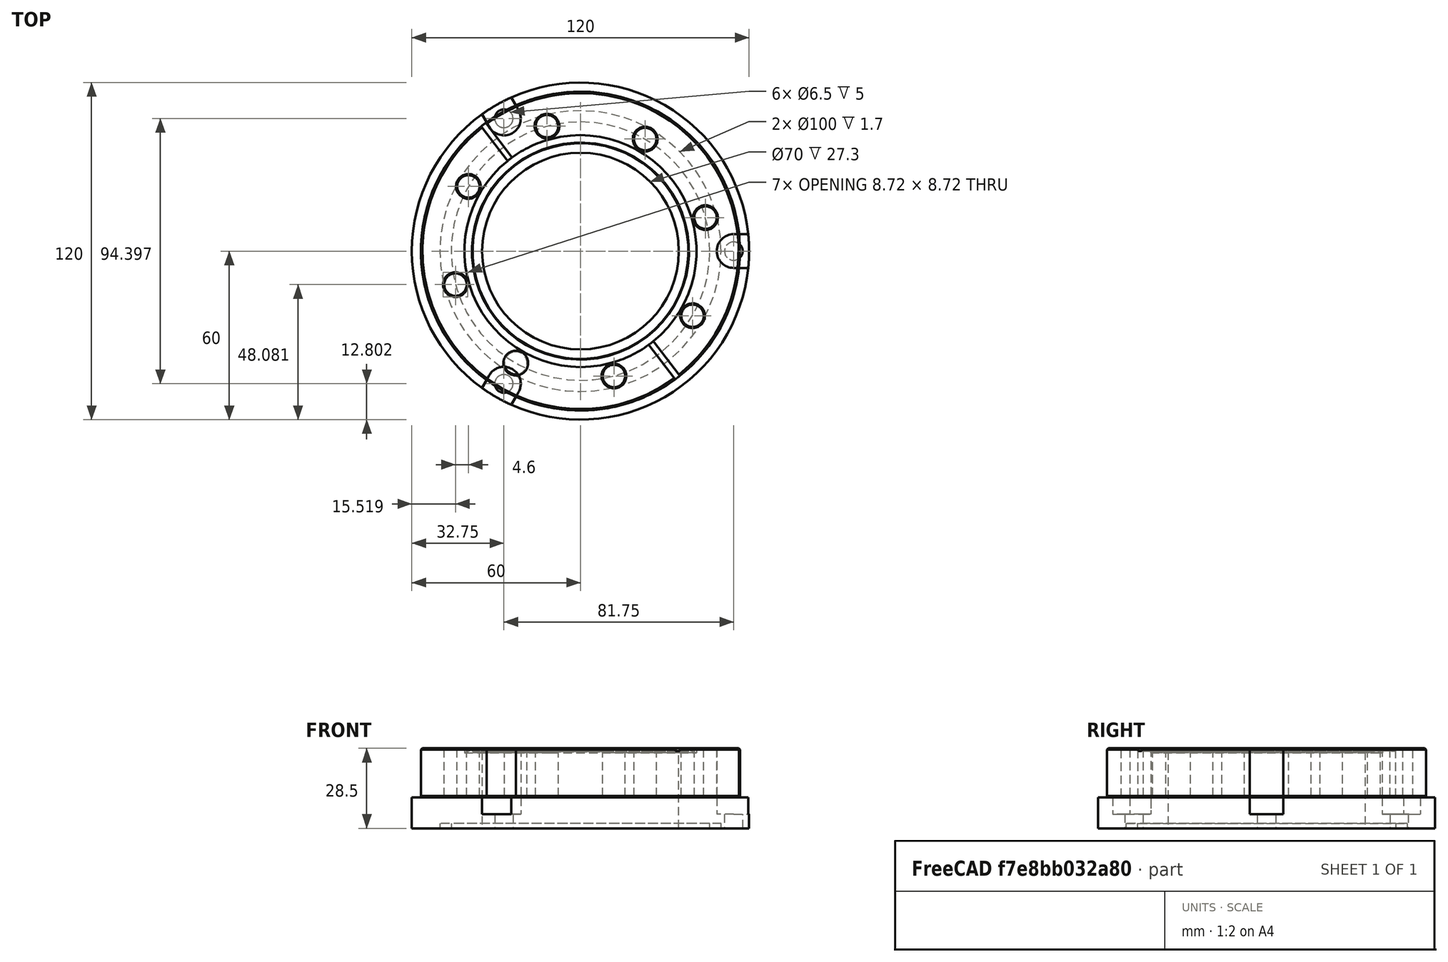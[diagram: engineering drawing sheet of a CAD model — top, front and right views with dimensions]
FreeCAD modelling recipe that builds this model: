
FCSTD DOCUMENT  (FreeCAD 0.21R33675 (Git))
Label: PhilippsXL30_FlangeToCF63_ZeroLengthAdapter_100
License: All rights reserved
LicenseURL: http://en.wikipedia.org/wiki/All_rights_reserved
objects: TechDraw::DrawViewDimension×32, Part::Cylinder×5, Part::MultiFuse×5, Part::Box×3, Part::Feature×3, Part::Compound×3, TechDraw::DrawProjGroupItem×3, TechDraw::DrawSVGTemplate×2, Part::Cut×2, TechDraw::DrawPage×2, App::Link×1, TechDraw::DrawProjGroup×1, TechDraw::DrawViewPart×1, TechDraw::DrawViewSection×1
note: 65 computed .brp shape members not serialized (recipe doc carries the construction recipe); baked Part::Feature solids carry a one-line shape summary decoded from their .brp
EXTERNAL_REF file=PhilippsXL30_Blindflange_120.FCStd obj=Cut003

FEATURE [App::Link] Link  label="Cut003"
  LinkedObject = -> <external PhilippsXL30_Blindflange_120.FCStd>#Cut003
FEATURE [Part::Box] Box  label="Würfel"
  AttacherType = Attacher::AttachEngine3D
  Height = 24
  Length = 10
  Placement = pos=(54.5,-6,5) rot=(0,0,1;0rad)
  Width = 12
FEATURE [Part::Cylinder] Cylinder  label="Zylinder"
  Angle = 360
  AttacherType = Attacher::AttachEngine3D
  FirstAngle = 0
  Height = 24
  Placement = pos=(54.5,0,5) rot=(0,0,1;0rad)
  Radius = 6
  SecondAngle = 0
FEATURE [Part::Box] Box001  label="Würfel001"
  AttacherType = Attacher::AttachEngine3D
  Height = 24
  Length = 10
  Placement = pos=(54.5,-6,5) rot=(0,0,1;0rad)
  Width = 12
FEATURE [Part::Cylinder] Cylinder001  label="Zylinder001"
  Angle = 360
  AttacherType = Attacher::AttachEngine3D
  FirstAngle = 0
  Height = 24
  Placement = pos=(54.5,0,5) rot=(0,0,1;0rad)
  Radius = 6
  SecondAngle = 0
FEATURE [Part::Box] Box002  label="Würfel002"
  AttacherType = Attacher::AttachEngine3D
  Height = 24
  Length = 10
  Placement = pos=(54.5,-6,5) rot=(0,0,1;0rad)
  Width = 12
FEATURE [Part::Cylinder] Cylinder002  label="Zylinder002"
  Angle = 360
  AttacherType = Attacher::AttachEngine3D
  FirstAngle = 0
  Height = 24
  Placement = pos=(54.5,0,5) rot=(0,0,1;0rad)
  Radius = 6
  SecondAngle = 0
FEATURE [Part::Feature] Link_solid  label="Cut003 (Solid)"
  shape: bbox 120 x 120 x 11 mm, 31 faces (baked)
FEATURE [Part::MultiFuse] Fusion001
  Shapes = -> [Box,Cylinder]
FEATURE [Part::MultiFuse] Fusion002
  Placement = pos=(0,0,0) rot=(0,0,1;2.0944rad)
  Shapes = -> [Box001,Cylinder001]
FEATURE [Part::MultiFuse] Fusion003
  Placement = pos=(0,0,0) rot=(0,0,1;4.18879rad)
  Shapes = -> [Box002,Cylinder002]
FEATURE [Part::Compound] Compound001
  Links = -> [Fusion001,Fusion002,Fusion003]
FEATURE [Part::Cylinder] Cylinder003  label="Zylinder003"
  Angle = 360
  AttacherType = Attacher::AttachEngine3D
  FirstAngle = 0
  Height = 23.5
  Placement = pos=(46.1,0,5) rot=(0,0,1;0rad)
  Radius = 4.8
  SecondAngle = 0
FEATURE [Part::Compound] Compound002
  Links = -> [Cylinder003]
  Placement = pos=(0,0,0) rot=(0,0,1;4.18879rad)
FEATURE [Part::Cylinder] Cylinder004  label="Zylinder004"
  Angle = 360
  AttacherType = Attacher::AttachEngine3D
  FirstAngle = 0
  Height = 50
  Radius = 35
  SecondAngle = 0
FEATURE [TechDraw::DrawSVGTemplate] Template
  EditableTexts = Designed_by_Name=Thomas Spielauer; FC-Date=2023-11-08; FC-SC=mm; FC-SH=1/2; FC-Title=120mm to CF63 adapter; Subtitle=XL30 ESEM compatible
  Height = 210
  Orientation = 1
  Template = <path>
  Width = 297
FEATURE [Part::Feature] Part__Feature001  label="Hositrad_CF63-BT"
  Placement = pos=(0,0,28.5) rot=(1,0,0;1.5708rad)
  shape: bbox 113.5 x 113.5 x 17.5 mm, 71 faces (baked)
FEATURE [Part::Compound] Compound
  Links = -> [Part__Feature001]
  Placement = pos=(0,0,0) rot=(0,0,1;0.261799rad)
FEATURE [Part::MultiFuse] Fusion
  Shapes = -> [Link_solid,Compound]
FEATURE [Part::Feature] Fusion_solid001  label="Fusion (Solid)001"
  shape: bbox 120 x 120 x 28.5 mm, 114 faces (baked)
FEATURE [Part::MultiFuse] Fusion004
  Shapes = -> [Compound002,Fusion_solid001]
FEATURE [Part::Cut] Cut
  Base = -> Fusion004
  Tool = -> Compound001
FEATURE [Part::Cut] Cut001
  Base = -> Cut
  Tool = -> Cylinder004
FEATURE [TechDraw::DrawProjGroupItem] ProjItem  label="Front"
  CoarseView = false
  Direction = (0,0,-1)
  Focus = 100
  HardHidden = false
  IsoCount = 0
  IsoHidden = false
  IsoVisible = false
  LockPosition = true
  Perspective = false
  Rotation = 0
  RotationVector = (0,1,0)
  Scale = 0.666667
  ScaleType = 2
  ScrubCount = 0
  SeamHidden = false
  SeamVisible = false
  SmoothHidden = false
  SmoothVisible = true
  Source = -> [Cut001]
  Type = 0
  X = 0
  XDirection = (0,1,0)
  Y = 0
FEATURE [TechDraw::DrawProjGroupItem] ProjItem001  label="Rear"
  CoarseView = false
  Direction = (0,0,1)
  Focus = 100
  HardHidden = false
  IsoCount = 0
  IsoHidden = false
  IsoVisible = false
  LockPosition = false
  Perspective = false
  Rotation = 0
  RotationVector = (1,0,0)
  Scale = 0.666667
  ScaleType = 2
  ScrubCount = 0
  SeamHidden = false
  SeamVisible = false
  SmoothHidden = false
  SmoothVisible = true
  Source = -> [Cut001]
  Type = 3
  X = 103.585
  XDirection = (0,-1,0)
  Y = 0
FEATURE [TechDraw::DrawProjGroupItem] ProjItem002  label="Top"
  CoarseView = false
  Direction = (1,0,0)
  Focus = 100
  HardHidden = false
  IsoCount = 0
  IsoHidden = false
  IsoVisible = false
  LockPosition = false
  Perspective = false
  Rotation = 0
  RotationVector = (1,0,0)
  Scale = 0.666667
  ScaleType = 2
  ScrubCount = 0
  SeamHidden = false
  SeamVisible = false
  SmoothHidden = false
  SmoothVisible = true
  Source = -> [Cut001]
  Type = 4
  X = 0
  XDirection = (0,1,0)
  Y = -91.1591
FEATURE [TechDraw::DrawProjGroup] ProjGroup
  Anchor = -> ProjItem
  AutoDistribute = false
  LockPosition = false
  ProjectionType = 0
  Rotation = 0
  Scale = 0.666667
  ScaleType = 2
  Source = -> [Cut001]
  Views = -> [ProjItem,ProjItem001,ProjItem002]
  X = 86.4871
  Y = 141.809
  spacingX = 15
  spacingY = 15
FEATURE [TechDraw::DrawViewDimension] Dimension
  AngleOverride = false
  Arbitrary = false
  ArbitraryTolerances = false
  EqualTolerance = true
  ExtensionAngle = 0
  FormatSpec = ⌀%.2w
  FormatSpecOverTolerance = %+.2w
  FormatSpecUnderTolerance = %+.2w
  Inverted = false
  LineAngle = 0
  LockPosition = false
  MeasureType = 1
  OverTolerance = 0
  References2D = -> [ProjItem]
  Rotation = 0
  ScaleType = 0
  TheoreticalExact = false
  Type = 5
  UnderTolerance = 0
  X = 13.273
  Y = 49.9319
FEATURE [TechDraw::DrawViewDimension] Dimension001
  AngleOverride = false
  Arbitrary = false
  ArbitraryTolerances = false
  EqualTolerance = true
  ExtensionAngle = 0
  FormatSpec = ⌀%.2w
  FormatSpecOverTolerance = %+.2w
  FormatSpecUnderTolerance = %+.2w
  Inverted = false
  LineAngle = 0
  LockPosition = false
  MeasureType = 1
  OverTolerance = 0
  References2D = -> [ProjItem]
  Rotation = 0
  ScaleType = 0
  TheoreticalExact = false
  Type = 5
  UnderTolerance = 0
  X = 24.0179
  Y = 47.193
FEATURE [TechDraw::DrawViewDimension] Dimension002
  AngleOverride = false
  Arbitrary = false
  ArbitraryTolerances = false
  EqualTolerance = true
  ExtensionAngle = 0
  FormatSpec = ⌀%.2w
  FormatSpecOverTolerance = %+.2w
  FormatSpecUnderTolerance = %+.2w
  Inverted = false
  LineAngle = 0
  LockPosition = false
  MeasureType = 1
  OverTolerance = 0
  References2D = -> [ProjItem]
  Rotation = 0
  ScaleType = 0
  TheoreticalExact = false
  Type = 5
  UnderTolerance = 0
  X = 30.1277
  Y = 42.7687
FEATURE [TechDraw::DrawViewDimension] Dimension003
  AngleOverride = false
  Arbitrary = false
  ArbitraryTolerances = false
  EqualTolerance = true
  ExtensionAngle = 0
  FormatSpec = ⌀%.2w
  FormatSpecOverTolerance = %+.2w
  FormatSpecUnderTolerance = %+.2w
  Inverted = false
  LineAngle = 0
  LockPosition = false
  MeasureType = 1
  OverTolerance = 0
  References2D = -> [ProjItem]
  Rotation = 0
  ScaleType = 0
  TheoreticalExact = false
  Type = 5
  UnderTolerance = 0
  X = 35.1841
  Y = 34.552
FEATURE [TechDraw::DrawViewDimension] Dimension004
  AngleOverride = false
  Arbitrary = false
  ArbitraryTolerances = false
  EqualTolerance = true
  ExtensionAngle = 0
  FormatSpec = ⌀%.2w
  FormatSpecOverTolerance = %+.2w
  FormatSpecUnderTolerance = %+.2w
  Inverted = false
  LineAngle = 0
  LockPosition = false
  MeasureType = 1
  OverTolerance = 0
  References2D = -> [ProjItem]
  Rotation = 0
  ScaleType = 0
  TheoreticalExact = false
  Type = 5
  UnderTolerance = 0
  X = 47.761
  Y = 10.7853
FEATURE [TechDraw::DrawViewDimension] Dimension005
  AngleOverride = false
  Arbitrary = false
  ArbitraryTolerances = false
  EqualTolerance = true
  ExtensionAngle = 0
  FormatSpec = %.2w
  FormatSpecOverTolerance = %+.2w
  FormatSpecUnderTolerance = %+.2w
  Inverted = false
  LineAngle = 0
  LockPosition = false
  MeasureType = 1
  OverTolerance = 0
  References2D = -> [ProjItem]
  Rotation = 0
  ScaleType = 0
  TheoreticalExact = false
  Type = 6
  UnderTolerance = 0
  X = 30.5032
  Y = -36.3658
FEATURE [TechDraw::DrawViewDimension] Dimension006
  AngleOverride = false
  Arbitrary = false
  ArbitraryTolerances = false
  EqualTolerance = true
  ExtensionAngle = 0
  FormatSpec = ⌀%.2w (3x)
  FormatSpecOverTolerance = %+.2w
  FormatSpecUnderTolerance = %+.2w
  Inverted = false
  LineAngle = 0
  LockPosition = false
  MeasureType = 1
  OverTolerance = 0
  References2D = -> [ProjItem]
  Rotation = 0
  ScaleType = 0
  TheoreticalExact = false
  Type = 5
  UnderTolerance = 0
  X = -27.3798
  Y = 53.7456
FEATURE [TechDraw::DrawViewDimension] Dimension007
  AngleOverride = false
  Arbitrary = false
  ArbitraryTolerances = false
  EqualTolerance = true
  ExtensionAngle = 0
  FormatSpec = ⌀%.2w
  FormatSpecOverTolerance = %+.2w
  FormatSpecUnderTolerance = %+.2w
  Inverted = false
  LineAngle = 0
  LockPosition = false
  MeasureType = 1
  OverTolerance = 0
  References2D = -> [ProjItem001]
  Rotation = 0
  ScaleType = 0
  TheoreticalExact = false
  Type = 5
  UnderTolerance = 0
  X = 51.25
  Y = 21.5576
FEATURE [TechDraw::DrawViewDimension] Dimension008
  AngleOverride = false
  Arbitrary = false
  ArbitraryTolerances = false
  EqualTolerance = true
  ExtensionAngle = 0
  FormatSpec = ⌀%.2w (CF63 knife)
  FormatSpecOverTolerance = %+.2w
  FormatSpecUnderTolerance = %+.2w
  Inverted = false
  LineAngle = 0
  LockPosition = false
  MeasureType = 1
  OverTolerance = 0
  References2D = -> [ProjItem001]
  Rotation = 0
  ScaleType = 0
  TheoreticalExact = false
  Type = 5
  UnderTolerance = 0
  X = 68.2486
  Y = 15.1076
FEATURE [TechDraw::DrawViewDimension] Dimension010
  AngleOverride = false
  Arbitrary = false
  ArbitraryTolerances = false
  EqualTolerance = true
  ExtensionAngle = 0
  FormatSpec = ⌀%.2w
  FormatSpecOverTolerance = %+.2w
  FormatSpecUnderTolerance = %+.2w
  Inverted = false
  LineAngle = 0
  LockPosition = false
  MeasureType = 1
  OverTolerance = 0
  References2D = -> [ProjItem001]
  Rotation = 0
  ScaleType = 0
  TheoreticalExact = false
  Type = 5
  UnderTolerance = 0
  X = 50.7383
  Y = -4.01857
FEATURE [TechDraw::DrawViewDimension] Dimension011
  AngleOverride = false
  Arbitrary = false
  ArbitraryTolerances = false
  EqualTolerance = true
  ExtensionAngle = 0
  FormatSpec = ⌀%+2w (7x M8)
  FormatSpecOverTolerance = %+.2w
  FormatSpecUnderTolerance = %+.2w
  Inverted = false
  LineAngle = 0
  LockPosition = false
  MeasureType = 1
  OverTolerance = 0
  References2D = -> [ProjItem001]
  Rotation = 0
  ScaleType = 0
  TheoreticalExact = false
  Type = 5
  UnderTolerance = 0
  X = 44.1386
  Y = 45.7398
FEATURE [TechDraw::DrawViewDimension] Dimension012
  AngleOverride = false
  Arbitrary = false
  ArbitraryTolerances = false
  EqualTolerance = true
  ExtensionAngle = 0
  FormatSpec = ⌀%.2w (ignore)
  FormatSpecOverTolerance = %+.2w
  FormatSpecUnderTolerance = %+.2w
  Inverted = false
  LineAngle = 0
  LockPosition = false
  MeasureType = 1
  OverTolerance = 0
  References2D = -> [ProjItem001]
  Rotation = 0
  ScaleType = 0
  TheoreticalExact = false
  Type = 5
  UnderTolerance = 0
  X = 56.2438
  Y = -18.0288
FEATURE [TechDraw::DrawViewDimension] Dimension013
  AngleOverride = false
  Arbitrary = false
  ArbitraryTolerances = false
  EqualTolerance = true
  ExtensionAngle = 0
  FormatSpec = ⌀%.2w (CF63 knife)
  FormatSpecOverTolerance = %+.2w
  FormatSpecUnderTolerance = %+.2w
  Inverted = false
  LineAngle = 0
  LockPosition = false
  MeasureType = 1
  OverTolerance = 0
  References2D = -> [ProjItem001]
  Rotation = 0
  ScaleType = 0
  TheoreticalExact = false
  Type = 5
  UnderTolerance = 0
  X = 69.1563
  Y = 3.81479
FEATURE [TechDraw::DrawViewDimension] Dimension014
  AngleOverride = false
  Arbitrary = false
  ArbitraryTolerances = false
  EqualTolerance = true
  ExtensionAngle = 0
  FormatSpec = ⌀%.2w
  FormatSpecOverTolerance = %+.2w
  FormatSpecUnderTolerance = %+.2w
  Inverted = false
  LineAngle = 0
  LockPosition = false
  MeasureType = 1
  OverTolerance = 0
  References2D = -> [ProjItem001]
  Rotation = 0
  ScaleType = 0
  TheoreticalExact = false
  Type = 5
  UnderTolerance = 0
  X = -46.1176
  Y = -23.6426
FEATURE [TechDraw::DrawViewDimension] Dimension015
  AngleOverride = false
  Arbitrary = false
  ArbitraryTolerances = false
  EqualTolerance = true
  ExtensionAngle = 0
  FormatSpec = ⌀%.2w
  FormatSpecOverTolerance = %+.2w
  FormatSpecUnderTolerance = %+.2w
  Inverted = false
  LineAngle = 0
  LockPosition = false
  MeasureType = 1
  OverTolerance = 0
  References2D = -> [ProjItem001]
  Rotation = 0
  ScaleType = 0
  TheoreticalExact = false
  Type = 5
  UnderTolerance = 0
  X = 58.2576
  Y = 40.308
FEATURE [TechDraw::DrawViewDimension] Dimension016
  AngleOverride = false
  Arbitrary = false
  ArbitraryTolerances = false
  EqualTolerance = true
  ExtensionAngle = 0
  FormatSpec = %.2w
  FormatSpecOverTolerance = %+.2w
  FormatSpecUnderTolerance = %+.2w
  Inverted = false
  LineAngle = 0
  LockPosition = false
  MeasureType = 1
  OverTolerance = 0
  References2D = -> [ProjItem001]
  Rotation = 0
  ScaleType = 0
  TheoreticalExact = false
  Type = 1
  UnderTolerance = 0
  X = 8.90961
  Y = 48.6597
FEATURE [TechDraw::DrawViewDimension] Dimension017
  AngleOverride = false
  Arbitrary = false
  ArbitraryTolerances = false
  EqualTolerance = true
  ExtensionAngle = 0
  FormatSpec = %.2w
  FormatSpecOverTolerance = %+.2w
  FormatSpecUnderTolerance = %+.2w
  Inverted = false
  LineAngle = 0
  LockPosition = false
  MeasureType = 1
  OverTolerance = 0
  References2D = -> [ProjItem002]
  Rotation = 0
  ScaleType = 0
  TheoreticalExact = false
  Type = 2
  UnderTolerance = 0
  X = -47.0367
  Y = -10.6679
FEATURE [TechDraw::DrawViewDimension] Dimension018
  AngleOverride = false
  Arbitrary = false
  ArbitraryTolerances = false
  EqualTolerance = true
  ExtensionAngle = 0
  FormatSpec = %.2w
  FormatSpecOverTolerance = %+.2w
  FormatSpecUnderTolerance = %+.2w
  Inverted = false
  LineAngle = 0
  LockPosition = false
  MeasureType = 1
  OverTolerance = 0
  References2D = -> [ProjItem002]
  Rotation = 0
  ScaleType = 0
  TheoreticalExact = false
  Type = 2
  UnderTolerance = 0
  X = -56.6562
  Y = 19.2142
FEATURE [TechDraw::DrawViewDimension] Dimension019
  AngleOverride = false
  Arbitrary = false
  ArbitraryTolerances = false
  EqualTolerance = true
  ExtensionAngle = 0
  FormatSpec = %.2w
  FormatSpecOverTolerance = %+.2w
  FormatSpecUnderTolerance = %+.2w
  Inverted = false
  LineAngle = 0
  LockPosition = false
  MeasureType = 1
  OverTolerance = 0
  References2D = -> [ProjItem002]
  Rotation = 0
  ScaleType = 0
  TheoreticalExact = false
  Type = 1
  UnderTolerance = 0
  X = 52.4225
  Y = -14.6035
FEATURE [TechDraw::DrawViewDimension] Dimension020
  AngleOverride = false
  Arbitrary = false
  ArbitraryTolerances = false
  EqualTolerance = true
  ExtensionAngle = 0
  FormatSpec = %.2w
  FormatSpecOverTolerance = %+.2w
  FormatSpecUnderTolerance = %+.2w
  Inverted = false
  LineAngle = 0
  LockPosition = false
  MeasureType = 1
  OverTolerance = 0
  References2D = -> [ProjItem002]
  Rotation = 0
  ScaleType = 0
  TheoreticalExact = false
  Type = 1
  UnderTolerance = 0
  X = 52.1421
  Y = 23.3431
FEATURE [TechDraw::DrawSVGTemplate] Template001
  EditableTexts = Designed_by_Name=Thomas Spielauer; FC-Date=2023-11-08; FC-SC=mm; FC-SH=2/2; FC-Title=120mm to CF63 adapter; Subtitle=XL30 ESEM compatible
  Height = 210
  Orientation = 1
  Template = <path>
  Width = 297
FEATURE [TechDraw::DrawViewPart] View
  CoarseView = false
  Direction = (0,0,1)
  Focus = 100
  HardHidden = false
  IsoCount = 0
  IsoHidden = false
  IsoVisible = false
  LockPosition = false
  Perspective = false
  Rotation = 90
  Scale = 0.5
  ScaleType = 2
  ScrubCount = 0
  SeamHidden = false
  SeamVisible = false
  SmoothHidden = false
  SmoothVisible = true
  Source = -> [Cut001]
  X = 66.9566
  XDirection = (0,1,0)
  Y = 53.8152
FEATURE [TechDraw::DrawViewSection] SectionView  label="Section  - "
  BaseView = -> View
  CoarseView = false
  CutSurfaceDisplay = 2
  Direction = (1e-16,-1,0)
  FileGeomPattern = <path>
  FileHatchPattern = <path>
  Focus = 100
  FuseBeforeCut = false
  HardHidden = false
  HatchOffset = (0,0,0)
  HatchRotation = 0
  HatchScale = 1
  IsoCount = 0
  IsoHidden = false
  IsoVisible = false
  LockPosition = false
  NameGeomPattern = Diamant
  Perspective = false
  Rotation = 0
  Scale = 1.8
  ScaleType = 2
  ScrubCount = 0
  SeamHidden = false
  SeamVisible = false
  SectionDirection = 4
  SectionNormal = (1e-16,-1,0)
  SectionOrigin = (0,0,14.25)
  SmoothHidden = false
  SmoothVisible = true
  Source = -> [Cut001]
  TrimAfterCut = false
  X = 151.069
  XDirection = (1,1e-16,0)
  Y = 145.819
FEATURE [TechDraw::DrawViewDimension] Dimension021
  AngleOverride = false
  Arbitrary = false
  ArbitraryTolerances = false
  EqualTolerance = true
  ExtensionAngle = 0
  FormatSpec = %.2w
  FormatSpecOverTolerance = %+.2w
  FormatSpecUnderTolerance = %+.2w
  Inverted = false
  LineAngle = 0
  LockPosition = false
  MeasureType = 1
  OverTolerance = 0
  References2D = -> [SectionView]
  Rotation = 0
  ScaleType = 0
  TheoreticalExact = false
  Type = 2
  UnderTolerance = 0
  X = -125.279
  Y = -30.3858
FEATURE [TechDraw::DrawViewDimension] Dimension022
  AngleOverride = false
  Arbitrary = false
  ArbitraryTolerances = false
  EqualTolerance = true
  ExtensionAngle = 0
  FormatSpec = %.2w
  FormatSpecOverTolerance = %+.2w
  FormatSpecUnderTolerance = %+.2w
  Inverted = false
  LineAngle = 0
  LockPosition = false
  MeasureType = 1
  OverTolerance = 0
  References2D = -> [SectionView]
  Rotation = 0
  ScaleType = 0
  TheoreticalExact = false
  Type = 1
  UnderTolerance = 0
  X = -77.5041
  Y = -37.296
FEATURE [TechDraw::DrawViewDimension] Dimension023
  AngleOverride = false
  Arbitrary = false
  ArbitraryTolerances = false
  EqualTolerance = true
  ExtensionAngle = 0
  FormatSpec = %.2w
  FormatSpecOverTolerance = %+.2w
  FormatSpecUnderTolerance = %+.2w
  Inverted = false
  LineAngle = 0
  LockPosition = false
  MeasureType = 1
  OverTolerance = 0
  References2D = -> [SectionView]
  Rotation = 0
  ScaleType = 0
  TheoreticalExact = false
  Type = 1
  UnderTolerance = 0
  X = -2.28943
  Y = 2.72866
FEATURE [TechDraw::DrawViewDimension] Dimension024
  AngleOverride = false
  Arbitrary = false
  ArbitraryTolerances = false
  EqualTolerance = true
  ExtensionAngle = 0
  FormatSpec = %.2w
  FormatSpecOverTolerance = %+.2w
  FormatSpecUnderTolerance = %+.2w
  Inverted = false
  LineAngle = 0
  LockPosition = false
  MeasureType = 1
  OverTolerance = 0
  References2D = -> [SectionView]
  Rotation = 0
  ScaleType = 0
  TheoreticalExact = false
  Type = 2
  UnderTolerance = 0
  X = 118.505
  Y = -8.38277
FEATURE [TechDraw::DrawViewDimension] Dimension025
  AngleOverride = false
  Arbitrary = false
  ArbitraryTolerances = false
  EqualTolerance = true
  ExtensionAngle = 0
  FormatSpec = %.2w
  FormatSpecOverTolerance = %+.2w
  FormatSpecUnderTolerance = %+.2w
  Inverted = false
  LineAngle = 0
  LockPosition = false
  MeasureType = 1
  OverTolerance = 0
  References2D = -> [SectionView]
  Rotation = 0
  ScaleType = 0
  TheoreticalExact = false
  Type = 1
  UnderTolerance = 0
  X = 122.168
  Y = -36.6638
FEATURE [TechDraw::DrawViewDimension] Dimension026
  AngleOverride = false
  Arbitrary = false
  ArbitraryTolerances = false
  EqualTolerance = true
  ExtensionAngle = 0
  FormatSpec = %.2w
  FormatSpecOverTolerance = %+.2w
  FormatSpecUnderTolerance = %+.2w
  Inverted = false
  LineAngle = 0
  LockPosition = false
  MeasureType = 1
  OverTolerance = 0
  References2D = -> [SectionView]
  Rotation = 0
  ScaleType = 0
  TheoreticalExact = false
  Type = 1
  UnderTolerance = 0
  X = 72.6138
  Y = -29.6388
FEATURE [TechDraw::DrawViewDimension] Dimension027
  AngleOverride = false
  Arbitrary = false
  ArbitraryTolerances = false
  EqualTolerance = true
  ExtensionAngle = 0
  FormatSpec = %.2w
  FormatSpecOverTolerance = %+.2w
  FormatSpecUnderTolerance = %+.2w
  Inverted = false
  LineAngle = 0
  LockPosition = false
  MeasureType = 1
  OverTolerance = 0
  References2D = -> [SectionView]
  Rotation = 0
  ScaleType = 0
  TheoreticalExact = false
  Type = 2
  UnderTolerance = 0
  X = -128.741
  Y = 38.2747
FEATURE [TechDraw::DrawViewDimension] Dimension028
  AngleOverride = false
  Arbitrary = false
  ArbitraryTolerances = false
  EqualTolerance = true
  ExtensionAngle = 0
  FormatSpec = %.2w
  FormatSpecOverTolerance = %+.2w
  FormatSpecUnderTolerance = %+.2w
  Inverted = false
  LineAngle = 0
  LockPosition = false
  MeasureType = 1
  OverTolerance = 0
  References2D = -> [SectionView]
  Rotation = 0
  ScaleType = 0
  TheoreticalExact = false
  Type = 2
  UnderTolerance = 0
  X = 0
  Y = 2.5
FEATURE [TechDraw::DrawViewDimension] Dimension029
  AngleOverride = false
  Arbitrary = false
  ArbitraryTolerances = false
  EqualTolerance = true
  ExtensionAngle = 0
  FormatSpec = %.2w
  FormatSpecOverTolerance = %+.2w
  FormatSpecUnderTolerance = %+.2w
  Inverted = false
  LineAngle = 0
  LockPosition = false
  MeasureType = 1
  OverTolerance = 0
  References2D = -> [SectionView]
  Rotation = 0
  ScaleType = 0
  TheoreticalExact = false
  Type = 2
  UnderTolerance = 0
  X = -120.766
  Y = 38.8741
FEATURE [TechDraw::DrawViewDimension] Dimension030
  AngleOverride = false
  Arbitrary = false
  ArbitraryTolerances = false
  EqualTolerance = true
  ExtensionAngle = 0
  FormatSpec = %.2w
  FormatSpecOverTolerance = %+.2w
  FormatSpecUnderTolerance = %+.2w
  Inverted = false
  LineAngle = 0
  LockPosition = false
  MeasureType = 1
  OverTolerance = 0
  References2D = -> [SectionView]
  Rotation = 0
  ScaleType = 0
  TheoreticalExact = false
  Type = 2
  UnderTolerance = 0
  X = -112.47
  Y = 38.1217
FEATURE [TechDraw::DrawViewDimension] Dimension031
  AngleOverride = false
  Arbitrary = false
  ArbitraryTolerances = false
  EqualTolerance = true
  ExtensionAngle = 0
  FormatSpec = %.2w (1mm deep leak checking groove)
  FormatSpecOverTolerance = %+.2w
  FormatSpecUnderTolerance = %+.2w
  Inverted = false
  LineAngle = 0
  LockPosition = false
  MeasureType = 1
  OverTolerance = 0
  References2D = -> [View]
  Rotation = 0
  ScaleType = 0
  TheoreticalExact = false
  Type = 0
  UnderTolerance = 0
  X = 63.3767
  Y = 6.5867
FEATURE [TechDraw::DrawPage] Page001
  KeepUpdated = true
  NextBalloonIndex = 1
  ProjectionType = 0
  Template = -> Template001
  Views = -> [View,SectionView,Dimension021,Dimension022,Dimension023,Dimension024,Dimension025,Dimension026,Dimension027,Dimension028,Dimension029,Dimension030,Dimension031]
FEATURE [TechDraw::DrawViewDimension] Dimension032
  AngleOverride = false
  Arbitrary = false
  ArbitraryTolerances = false
  EqualTolerance = true
  ExtensionAngle = 0
  FormatSpec = ⌀%.2w
  FormatSpecOverTolerance = %+.2w
  FormatSpecUnderTolerance = %+.2w
  Inverted = false
  LineAngle = 0
  LockPosition = false
  MeasureType = 1
  OverTolerance = 0
  References2D = -> [ProjItem001]
  Rotation = 0
  ScaleType = 0
  TheoreticalExact = false
  Type = 5
  UnderTolerance = 0
  X = 37.5059
  Y = -33.9713
FEATURE [TechDraw::DrawPage] Page
  KeepUpdated = true
  NextBalloonIndex = 1
  ProjectionType = 0
  Template = -> Template
  Views = -> [ProjGroup,Dimension,Dimension001,Dimension002,Dimension003,Dimension004,Dimension005,Dimension006,Dimension007,Dimension008,Dimension010,Dimension011,Dimension012,Dimension013,Dimension014,Dimension015,Dimension016,Dimension017,Dimension018,Dimension019,Dimension020,Dimension032]
note: 4 file-system paths scrubbed to <path> (originals preserved in the JSON sidecar)
